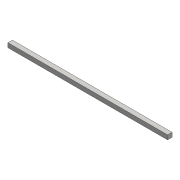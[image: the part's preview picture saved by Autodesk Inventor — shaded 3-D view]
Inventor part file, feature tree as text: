
AUTODESK INVENTOR PART (.ipt)
format: ipt  version: 2016 (Build 200138000, 138)  size: 67,072 bytes
history: native  units: mm
features: extrude x1, sketch x1
ambient origin geometry x8: Origin, YZ Plane, XZ Plane, XY Plane, X Axis, Y Axis, Z Axis, Center Point
bodies: Solid1 (feature_tree)
feature tree (2):
  extrude  "Extrusion1"  Depth=12.7mm
  sketch  "Sketch1"  dims[d0=12.7mm d1=12.7mm d2=457.2mm d3=0.0mm]
